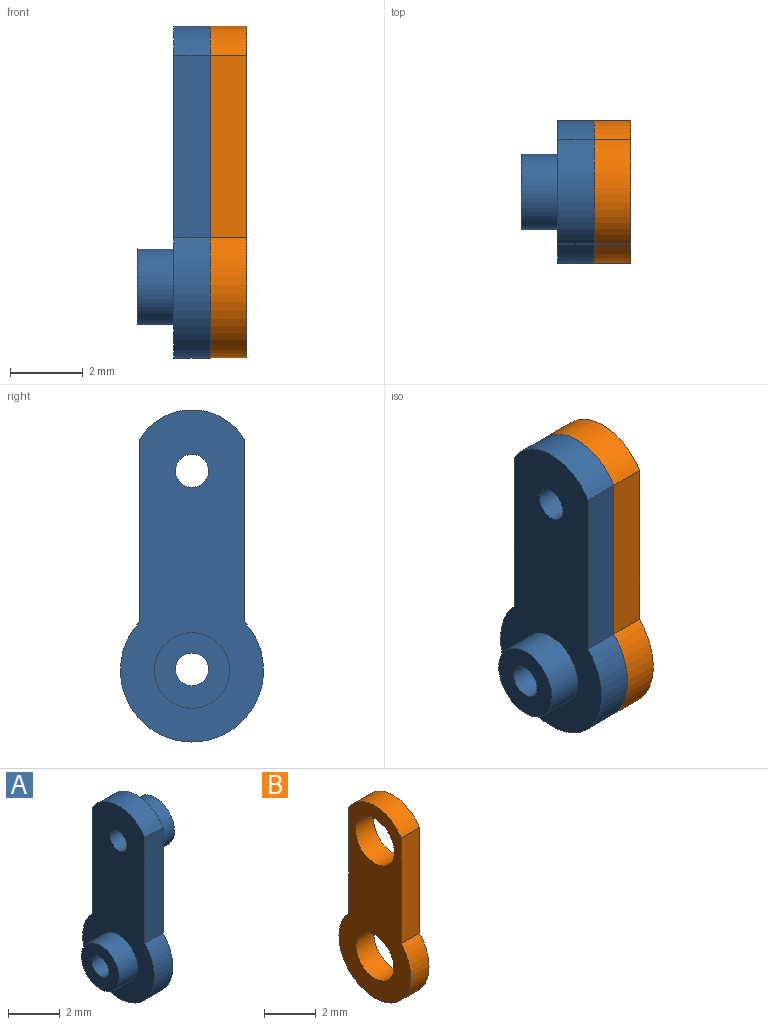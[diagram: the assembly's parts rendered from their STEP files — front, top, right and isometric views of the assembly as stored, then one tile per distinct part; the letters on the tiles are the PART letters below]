
ASSEMBLY  parts=2 mates=1
PART A: 12 faces, bbox 3x3.9x9.1 mm
  f0: plane 5x1mm, normal (0,1,0), area 5mm2, adj f1,f3,f4,f5
  f1: cylinder r=1.67mm len=2.87mm, axis (1,0,0), area 3.4mm2, adj f0,f2,f4,f5
  f2: plane 5x1mm, normal (0,-1,0), area 5mm2, adj f1,f3,f4,f5
  f3: cylinder r=1.96mm len=3.93mm, axis (1,0,0), area 9.1mm2, adj f0,f2,f4,f5
  f4: plane 9.12x3.93mm, normal (-1,0,0), area 22.9mm2, adj f0,f1,f2,f3,f8,f11
  f5: plane 9.12x3.93mm, normal (1,0,0), area 22.7mm2, adj f0,f1,f2,f3,f6,f10
  f6: cylinder r=1.06mm len=2.12mm, axis (-1,0,0), area 6.7mm2, adj f5,f7
  f7: plane 2.12x2.12mm, normal (1,0,0), area 2.9mm2, adj f6,f11
  f8: cylinder r=1.04mm len=2.07mm, axis (1,0,0), area 6.5mm2, adj f4,f9
  f9: plane 2.07x2.07mm, normal (-1,0,0), area 2.7mm2, adj f8,f10
  f10: cylinder r=0.45mm len=2mm, axis (1,0,0), area 5.7mm2, adj f5,f9
  f11: cylinder r=0.45mm len=2mm, axis (1,0,0), area 5.7mm2, adj f4,f7
PART B: 8 faces, bbox 1x3.9x9.1 mm
  f0: plane 5x1mm, normal (0,1,0), area 5mm2, adj f1,f4,f6,f7
  f1: cylinder r=1.67mm len=2.87mm, axis (-1,0,0), area 3.4mm2, adj f0,f2,f6,f7
  f2: plane 5x1mm, normal (0,-1,0), area 5mm2, adj f1,f4,f6,f7
  f3: cylinder r=1.06mm len=2.12mm, axis (-1,0,0), area 6.7mm2, adj f6,f7
  f4: cylinder r=1.96mm len=3.93mm, axis (-1,0,0), area 9.1mm2, adj f0,f2,f6,f7
  f5: cylinder r=1.04mm len=2.07mm, axis (-1,0,0), area 6.5mm2, adj f6,f7
  f6: plane 9.12x3.93mm, normal (1,0,0), area 20mm2, adj f0,f1,f2,f3,f4,f5
  f7: plane 9.12x3.93mm, normal (-1,0,0), area 20mm2, adj f0,f1,f2,f3,f4,f5
PLACE A t=(0.53,1.54,2.59)mm
PLACE B t=(0.53,1.54,2.59)mm
MATE revolute B.f3 <-> A.f6  axis (-1,0,0) through (1.53,1.54,16.88)mm
